# Revit family: MC-15D-HS
name_source: partatom
category: Plumbing Fixtures
revit_build: Autodesk Revit 2018 (Build: 20170223_1515(x64)
units: mm (PartAtom-declared; Revit-internal decimal feet)

## family parameters
Cut with Voids When Loaded = No
Host = Face
OmniClass Number = 23.45.05.21.11
OmniClass Title = Water Closets
Part Type = Normal
Room Calculation Point = No
Round Connector Dimension = Use Diameter
Shared = No

## types (1)
- MC-15D-HS
    Cast Iron waste Dia = 0' - 4"
    Default Elevation = 0' - 0"
    Description = DOUBLE FIXED VERTICAL HUB AND SPIGOT WATER CLOSET CARRIER OFFSET FROM STACK
    Floor Drain Material = Paint - Sherwin Williams Paint - #952C2A - Bellwood Red
    Inlet To Floor Height = 0' - 9 1/2"
    MC-15L-HS = Yes
    MC-15R-HS = Yes
    Manufacturer = MIFAB
    Model = MC-15D-HS
    URL = WWW.MIFAB.COM
    Vent Dia = 0' - 2"
    WFU = 0

## geometry (parser evidence)
native form markers: Blend x2, Sweep x4
no freeform markers — native parametric forms only
